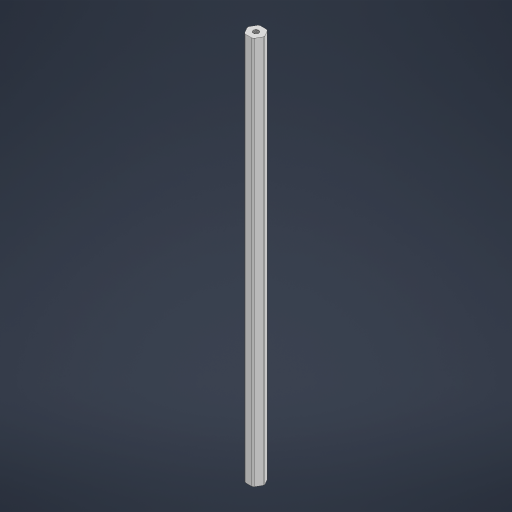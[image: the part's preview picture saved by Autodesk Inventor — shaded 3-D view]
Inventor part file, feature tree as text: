
AUTODESK INVENTOR PART (.ipt)
format: ipt  version: 2023 (Build 270158000, 158)  size: 757,760 bytes
history: native  units: in
note: dims shown in document units (in); Inventor stores cm internally (conversion verified against a paired STEP export)
features: mirror x1
ambient origin geometry x8: Origin, YZ Plane, XZ Plane, XY Plane, X Axis, Y Axis, Z Axis, Center Point
bodies: Solid1 (feature_tree)
feature tree (1):
  mirror  "Mirror2"
